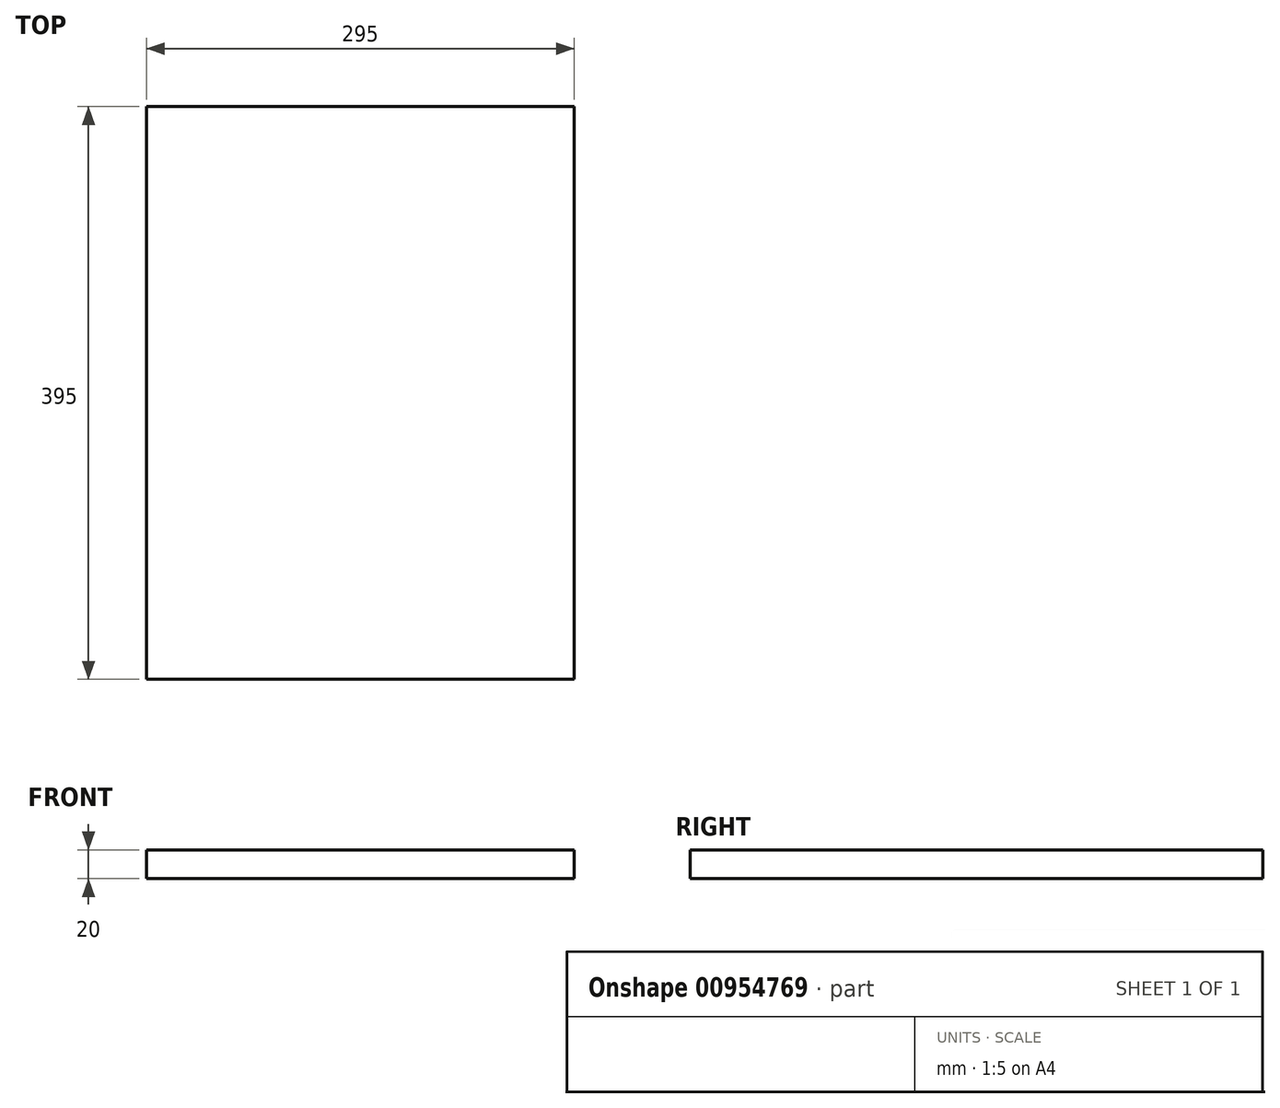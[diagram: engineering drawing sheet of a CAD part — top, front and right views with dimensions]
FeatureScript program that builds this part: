
annotation { "Feature Type Name" : "Feature", "Feature Type Description" : "" }
export const myFeature = defineFeature(function(context is Context, id is Id, definition is map)
    precondition{}
    {
        {
            var Q0;
            Q0=qCreatedBy(makeId("Top.planeOp"),FACE);
            var sketch = newSketch(context, id + "F0", { "sketchPlane" : qUnion([Q0])});
            skLineSegment(sketch, "E0.bottom", {"start": v(-147.5, 197.5) * mm, "end": v(147.5, 197.5) * mm});
            skLineSegment(sketch, "E0.top", {"start": v(-147.5, -197.5) * mm, "end": v(147.5, -197.5) * mm});
            skLineSegment(sketch, "E0.left", {"start": v(-147.5, 197.5) * mm, "end": v(-147.5, -197.5) * mm});
            skLineSegment(sketch, "E0.right", {"start": v(147.5, 197.5) * mm, "end": v(147.5, -197.5) * mm});
            skPoint(sketch, "E0.middle", {"position": v(0, 0) * mm});
            skSolve(sketch);
        }
        {
            var Q0;
            Q0=makeQuery(id+"F0.imprint","IMPRINT",FACE,{"disambiguationData":[TD([[makeQuery(id+"F0.imprint","IMPRINT",EDGE,{"derivedFrom":sQuery(id+"F0.wireOp",EDGE,"E0.bottom")}),-1.0]])]});
            extrude(context, id + "F1", {"entities" : qUnion([Q0]), "depth" : 20 * mm, "offsetDistance" : 25 * mm});
        }
    });
